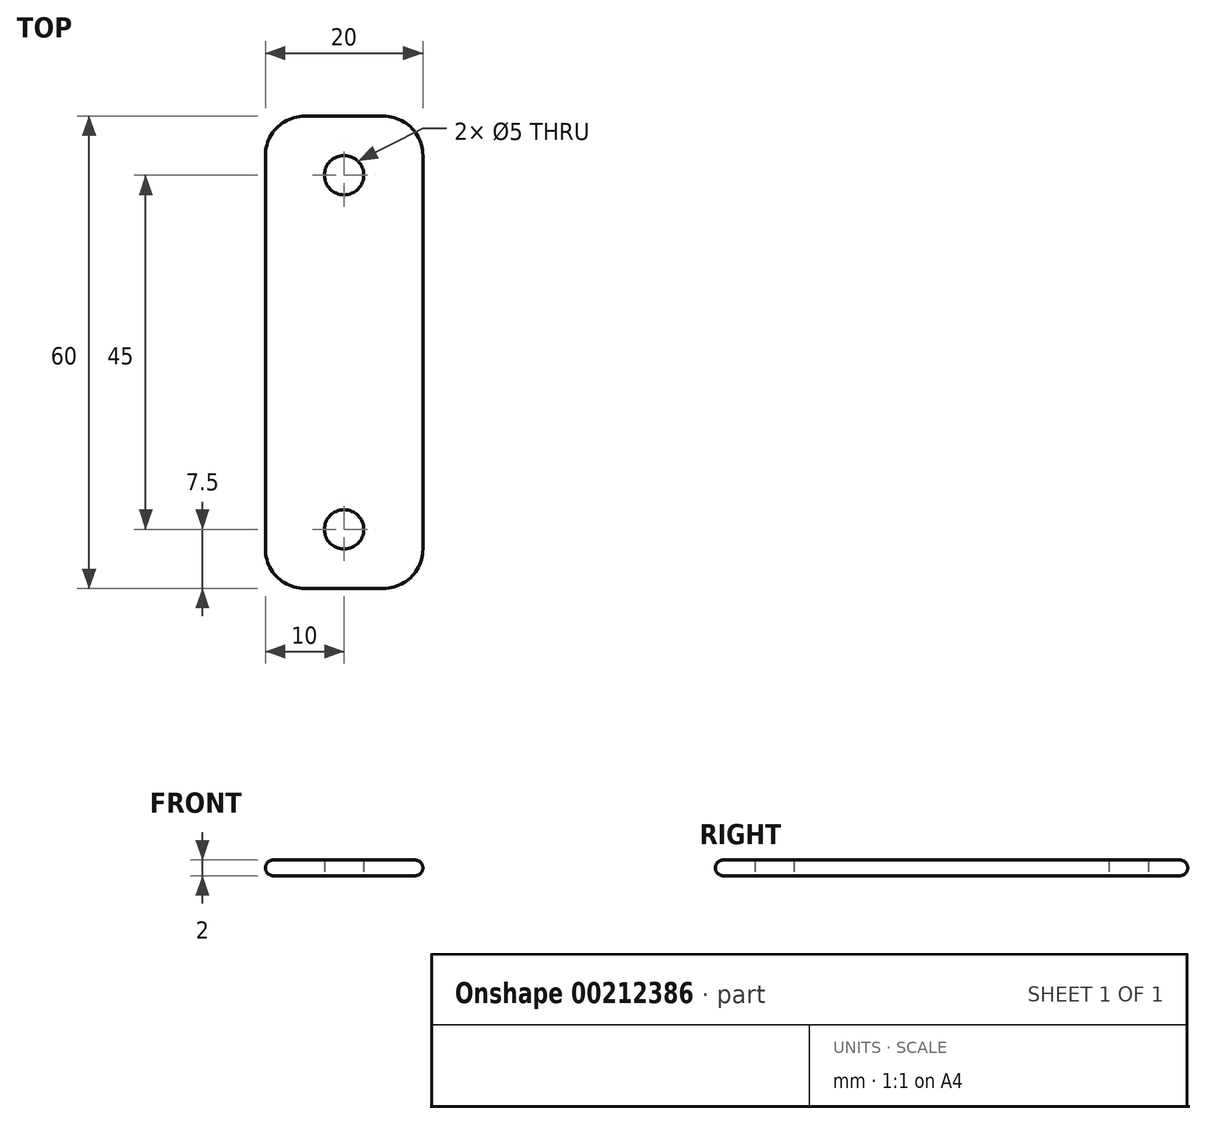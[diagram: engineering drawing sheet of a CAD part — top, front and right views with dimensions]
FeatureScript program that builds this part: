
annotation { "Feature Type Name" : "Feature", "Feature Type Description" : "" }
export const myFeature = defineFeature(function(context is Context, id is Id, definition is map)
    precondition{}
    {
        {
            var Q0;
            Q0=qCreatedBy(makeId("Top.planeOp"),FACE);
            var sketch = newSketch(context, id + "F0", { "sketchPlane" : qUnion([Q0])});
            skLineSegment(sketch, "E0.bottom", {"start": v(-5, 30) * mm, "end": v(5, 30) * mm});
            skLineSegment(sketch, "E0.top", {"start": v(-5, -30) * mm, "end": v(5, -30) * mm});
            skLineSegment(sketch, "E0.left", {"start": v(-10, 25) * mm, "end": v(-10, -25) * mm});
            skLineSegment(sketch, "E0.right", {"start": v(10, 25) * mm, "end": v(10, -25) * mm});
            skPoint(sketch, "E0.middle", {"position": v(0, 0) * mm});
            skPoint(sketch, "E1.visualSharp", {"position": v(-10, 30) * mm});
            skArc(sketch, "E1.filletArc", {"start": v(-5, 30) * mm, "mid": v(-8.54, 28.54) * mm, "end": v(-10, 25) * mm});
            skPoint(sketch, "E2.visualSharp", {"position": v(10, 30) * mm});
            skArc(sketch, "E2.filletArc", {"start": v(10, 25) * mm, "mid": v(8.54, 28.54) * mm, "end": v(5, 30) * mm});
            skPoint(sketch, "E3.visualSharp", {"position": v(-10, -30) * mm});
            skArc(sketch, "E3.filletArc", {"start": v(-10, -25) * mm, "mid": v(-8.54, -28.54) * mm, "end": v(-5, -30) * mm});
            skPoint(sketch, "E4.visualSharp", {"position": v(10, -30) * mm});
            skArc(sketch, "E4.filletArc", {"start": v(5, -30) * mm, "mid": v(8.54, -28.54) * mm, "end": v(10, -25) * mm});
            skCircle(sketch, "E5", {"center": v(0, 22.5) * mm, "radius": 2.5 * mm});
            skCircle(sketch, "E6", {"center": v(0, -22.5) * mm, "radius": 2.5 * mm});
            skSolve(sketch);
        }
        {
            var Q0;
            Q0=makeQuery(id+"F0.imprint","IMPRINT",FACE,{"disambiguationData":[TD([[makeQuery(id+"F0.imprint","IMPRINT",EDGE,{"derivedFrom":sQuery(id+"F0.wireOp",EDGE,"E0.bottom")}),-1.0]])]});
            extrude(context, id + "F1", {"entities" : qUnion([Q0]), "depth" : 2 * mm});
        }
        {
            var Q0;
            Q0=makeQuery(id+"F1.opExtrude","CAP_EDGE",EDGE,{"disambiguationData":[OSD([sQuery(id+"F0.wireOp",EDGE,"E0.right")])],"isStart":true});
            var Q1;
            Q1=makeQuery(id+"F1.opExtrude","CAP_EDGE",EDGE,{"disambiguationData":[OSD([sQuery(id+"F0.wireOp",EDGE,"E0.right")])],"isStart":false});
            fillet(context, id + "F2", {"entities" : qUnion([Q0, Q1]), "radius" : 1 * mm, "tangentPropagation" : true, "allowEdgeOverflow" : false});
        }
    });
